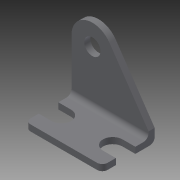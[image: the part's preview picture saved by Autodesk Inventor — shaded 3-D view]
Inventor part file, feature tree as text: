
AUTODESK INVENTOR PART (.ipt)
format: ipt  version: 2014 (Build 180170000, 170)  size: 195,072 bytes
history: native  units: in
note: dims shown in document units (in); Inventor stores cm internally (conversion verified against a paired STEP export)
features: other x161, sketch x8, extrude x5, hole x3
ambient origin geometry x8: Origin, YZ Plane, XZ Plane, XY Plane, X Axis, Y Axis, Z Axis, Center Point
bodies: Solid1 (feature_tree)
feature tree (177):
  extrude  "Extrusion1"  Depth=0.51in TaperAngle=0.0deg
  extrude  "Extrusion2"  Depth=0.0598in TaperAngle=0.0deg
  hole  "Hole1"  [1 undecoded]
  hole  "Hole2"  [1 undecoded]
  hole  "Hole3"  [1 undecoded]
  sketch  "Sketch_6"
  sketch  "Sketch_7"
  extrude  "Extrusion3"  [1 undecoded]
  extrude  "Extrusion4"  [1 undecoded]
  extrude  "Extrusion5"  [1 undecoded]
  other  "a1_XY"
  other  "a1_YZ"
  other  "a1_ZX"
  other  "a1_X"
  other  "a1_Y"
  other  "a1_Z"
  other  "a1_Center"
  other  "a2_XY"
  other  "a2_YZ"
  other  "a2_ZX"
  other  "a2_X"
  other  "a2_Y"
  other  "a2_Z"
  other  "a2_Center"
  other  "b1_XY"
  other  "b1_YZ"
  other  "b1_ZX"
  other  "b1_X"
  other  "b1_Y"
  other  "b1_Z"
  other  "b1_Center"
  other  "b2_XY"
  other  "b2_YZ"
  other  "b2_ZX"
  other  "b2_X"
  other  "b2_Y"
  other  "b2_Z"
  other  "b2_Center"
  other  "c1_XY"
  other  "c1_YZ"
  other  "c1_ZX"
  other  "c1_X"
  other  "c1_Y"
  other  "c1_Z"
  other  "c1_Center"
  other  "d1_XY"
  other  "d1_YZ"
  other  "d1_ZX"
  other  "d1_X"
  other  "d1_Y"
  other  "d1_Z"
  other  "d1_Center"
  other  "d2_XY"
  other  "d2_YZ"
  other  "d2_ZX"
  other  "d2_X"
  other  "d2_Y"
  other  "d2_Z"
  other  "d2_Center"
  other  "e1_XY"
  other  "e1_YZ"
  other  "e1_ZX"
  other  "e1_X"
  other  "e1_Y"
  other  "e1_Z"
  other  "e1_Center"
  other  "e2_XY"
  other  "e2_YZ"
  other  "e2_ZX"
  other  "e2_X"
  other  "e2_Y"
  other  "e2_Z"
  other  "e2_Center"
  other  "f1_XY"
  other  "f1_YZ"
  other  "f1_ZX"
  other  "f1_X"
  other  "f1_Y"
  other  "f1_Z"
  other  "f1_Center"
  other  "f2_XY"
  other  "f2_YZ"
  other  "f2_ZX"
  other  "f2_X"
  other  "f2_Y"
  other  "f2_Z"
  other  "f2_Center"
  other  "g1_XY"
  other  "g1_YZ"
  other  "g1_ZX"
  other  "g1_X"
  other  "g1_Y"
  other  "g1_Z"
  other  "g1_Center"
  other  "g2_XY"
  other  "g2_YZ"
  other  "g2_ZX"
  other  "g2_X"
  other  "g2_Y"
  other  "g2_Z"
  other  "g2_Center"
  other  "h1_XY"
  other  "h1_YZ"
  other  "h1_ZX"
  other  "h1_X"
  other  "h1_Y"
  other  "h1_Z"
  other  "h1_Center"
  other  "h2_XY"
  other  "h2_YZ"
  other  "h2_ZX"
  other  "h2_X"
  other  "h2_Y"
  other  "h2_Z"
  other  "h2_Center"
  other  "i_XY"
  other  "i_YZ"
  other  "i_ZX"
  other  "i_X"
  other  "i_Y"
  other  "i_Z"
  other  "i_Center"
  other  "j1_XY"
  other  "j1_YZ"
  other  "j1_ZX"
  other  "j1_X"
  other  "j1_Y"
  other  "j1_Z"
  other  "j1_Center"
  other  "j2_XY"
  other  "j2_YZ"
  other  "j2_ZX"
  other  "j2_X"
  other  "j2_Y"
  other  "j2_Z"
  other  "j2_Center"
  other  "k1_XY"
  other  "k1_YZ"
  other  "k1_ZX"
  other  "k1_X"
  other  "k1_Y"
  other  "k1_Z"
  other  "k1_Center"
  other  "k11_XY"
  other  "k11_YZ"
  other  "k11_ZX"
  other  "k11_X"
  other  "k11_Y"
  other  "k11_Z"
  other  "k11_Center"
  other  "k12_XY"
  other  "k12_YZ"
  other  "k12_ZX"
  other  "k12_X"
  other  "k12_Y"
  other  "k12_Z"
  other  "k12_Center"
  other  "to_dummy_L_XY"
  other  "to_dummy_L_YZ"
  other  "to_dummy_L_ZX"
  other  "to_dummy_L_X"
  other  "to_dummy_L_Y"
  other  "to_dummy_L_Z"
  other  "to_dummy_L_Center"
  other  "to_pin_L_XY"
  other  "to_pin_L_YZ"
  other  "to_pin_L_ZX"
  other  "to_pin_L_X"
  other  "to_pin_L_Y"
  other  "to_pin_L_Z"
  other  "to_pin_L_Center"
  sketch  "Sketch_1"  dims[d0=0.75in d1=0.0in d2=0.51in d3=0.0in]
  sketch  "Sketch_2"  dims[d4=0.1585in d5=0.75in d6=0.375in d7=0.25in d8=0.5635in d9=0.0598in d10=0.0in]
  sketch  "Sketch3"  dims[d11=0.19in d12=0.75in d13=0.375in d14=0.25in d15=0.5635in d16=0.0598in d17=0.0in]
  sketch  "Sketch4"  dims[d18=0.19in d19=0.75in d20=0.375in d21=0.25in d22=0.5635in d23=0.0598in d24=0.0in d25=0.0598in d26=0.0in]
  sketch  "Sketch5"  dims[d27=0.0598in d28=0.0in d29=0.0598in d30=0.0in]
  sketch  "Sketch_8"
note: 6 required parameter values undecoded (feature->parameter linkage not recoverable at this tier; creation-order binding heuristic only, values carry confidence <= 0.55)
